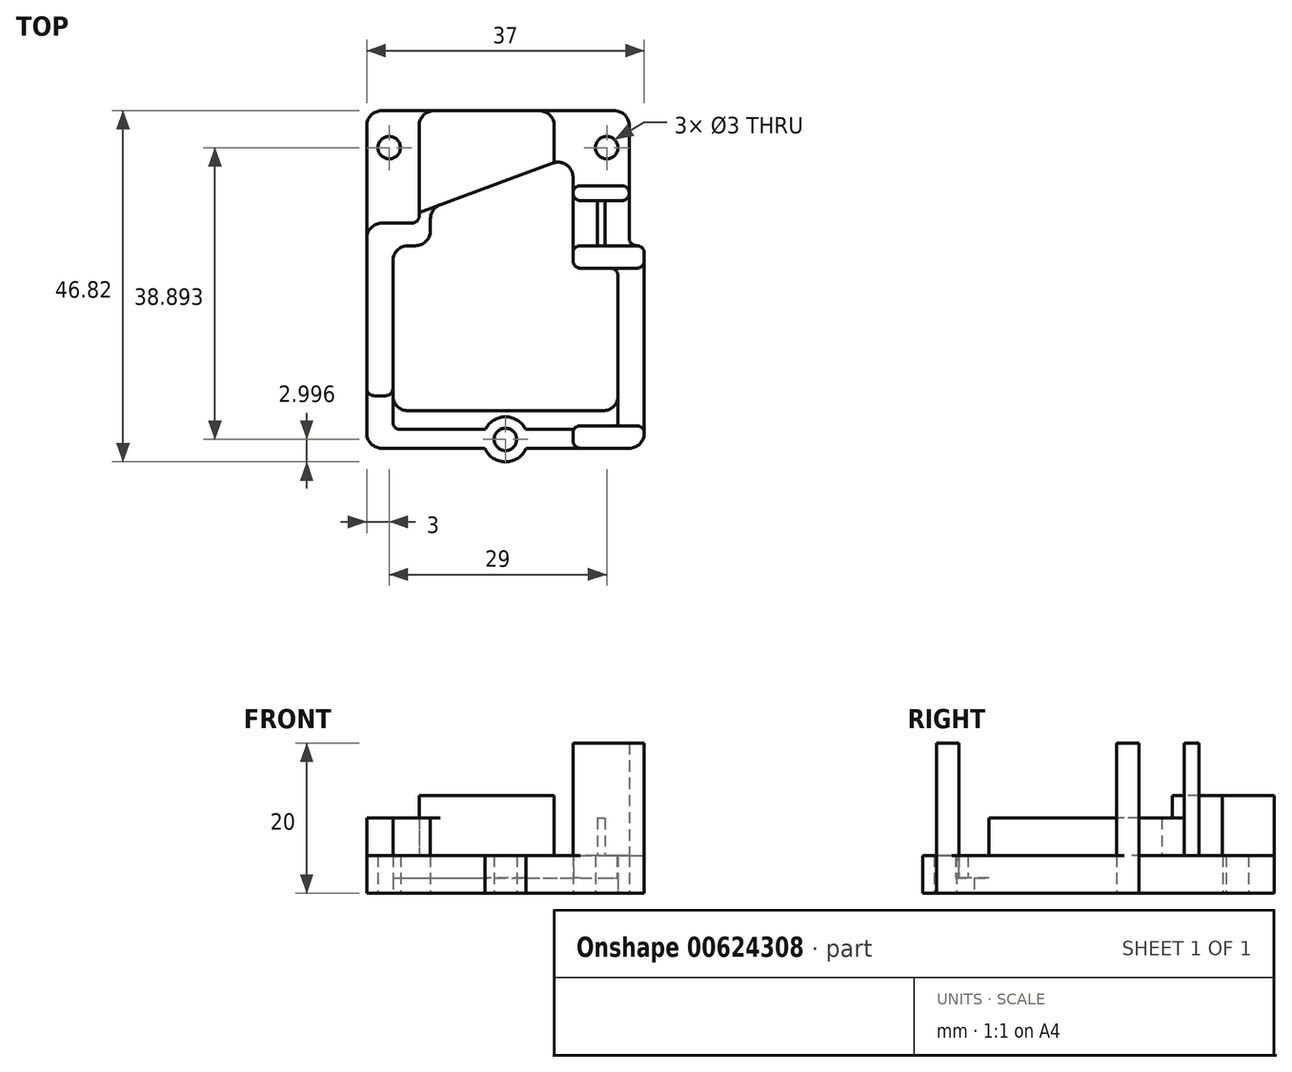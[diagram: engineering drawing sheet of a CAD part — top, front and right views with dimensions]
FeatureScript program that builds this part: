
annotation { "Feature Type Name" : "Feature", "Feature Type Description" : "" }
export const myFeature = defineFeature(function(context is Context, id is Id, definition is map)
    precondition{}
    {
        {
            var Q0;
            Q0=qCreatedBy(makeId("Top.planeOp"),FACE);
            var sketch = newSketch(context, id + "F0", { "sketchPlane" : qUnion([Q0])});
            skLineSegment(sketch, "E0.bottom", {"start": v(16.5, -22.5) * mm, "end": v(-16.5, -22.5) * mm});
            skLineSegment(sketch, "E0.top", {"start": v(14.5, 22.5) * mm, "end": v(-16.5, 22.5) * mm});
            skLineSegment(sketch, "E0.left", {"start": v(18.5, -20.5) * mm, "end": v(18.5, 3.5) * mm});
            skLineSegment(sketch, "E0.right", {"start": v(-18.5, -20.5) * mm, "end": v(-18.5, 20.5) * mm});
            skPoint(sketch, "E0.middle", {"position": v(0, 0) * mm});
            skLineSegment(sketch, "E1", {"start": v(-15, 2.5) * mm, "end": v(-15, -15.5) * mm});
            skLineSegment(sketch, "E2", {"start": v(-13, -17.5) * mm, "end": v(13, -17.5) * mm});
            skLineSegment(sketch, "E3", {"start": v(15, -15.5) * mm, "end": v(15, 0.5) * mm});
            skLineSegment(sketch, "E4", {"start": v(-13, 4.5) * mm, "end": v(-12, 4.5) * mm});
            skLineSegment(sketch, "E5", {"start": v(-10, 6.5) * mm, "end": v(-10, 8.1) * mm});
            skLineSegment(sketch, "E6", {"start": v(-8.7, 9.98) * mm, "end": v(6.3, 15.5) * mm});
            skLineSegment(sketch, "E7", {"start": v(9, 13.63) * mm, "end": v(9, 2.5) * mm});
            skLineSegment(sketch, "E8", {"start": v(10, 1.5) * mm, "end": v(14, 1.5) * mm});
            skLineSegment(sketch, "E9", {"start": v(16.5, 20.5) * mm, "end": v(16.5, 5.5) * mm});
            skLineSegment(sketch, "E10", {"start": v(17.5, 4.5) * mm, "end": v(17.5, 4.5) * mm});
            skPoint(sketch, "E11.visualSharp", {"position": v(-15, -17.5) * mm});
            skArc(sketch, "E11.filletArc", {"start": v(-15, -15.5) * mm, "mid": v(-14.41, -16.91) * mm, "end": v(-13, -17.5) * mm});
            skPoint(sketch, "E12.visualSharp", {"position": v(15, -17.5) * mm});
            skArc(sketch, "E12.filletArc", {"start": v(13, -17.5) * mm, "mid": v(14.41, -16.91) * mm, "end": v(15, -15.5) * mm});
            skPoint(sketch, "E13.visualSharp", {"position": v(-15, 4.5) * mm});
            skArc(sketch, "E13.filletArc", {"start": v(-13, 4.5) * mm, "mid": v(-14.41, 3.91) * mm, "end": v(-15, 2.5) * mm});
            skPoint(sketch, "E14.visualSharp", {"position": v(-10, 4.5) * mm});
            skArc(sketch, "E14.filletArc", {"start": v(-12, 4.5) * mm, "mid": v(-10.59, 5.09) * mm, "end": v(-10, 6.5) * mm});
            skPoint(sketch, "E15.visualSharp", {"position": v(-10, 9.5) * mm});
            skArc(sketch, "E15.filletArc", {"start": v(-8.7, 9.98) * mm, "mid": v(-9.64, 9.25) * mm, "end": v(-10, 8.1) * mm});
            skPoint(sketch, "E16.visualSharp", {"position": v(9, 16.5) * mm});
            skArc(sketch, "E16.filletArc", {"start": v(9, 13.63) * mm, "mid": v(8.14, 15.27) * mm, "end": v(6.3, 15.5) * mm});
            skPoint(sketch, "E17.visualSharp", {"position": v(-18.5, 22.5) * mm});
            skArc(sketch, "E17.filletArc", {"start": v(-16.5, 22.5) * mm, "mid": v(-17.91, 21.91) * mm, "end": v(-18.5, 20.5) * mm});
            skPoint(sketch, "E18.visualSharp", {"position": v(16.5, 22.5) * mm});
            skArc(sketch, "E18.filletArc", {"start": v(16.5, 20.5) * mm, "mid": v(15.91, 21.91) * mm, "end": v(14.5, 22.5) * mm});
            skPoint(sketch, "E19.visualSharp", {"position": v(18.5, -22.5) * mm});
            skArc(sketch, "E19.filletArc", {"start": v(16.5, -22.5) * mm, "mid": v(17.91, -21.91) * mm, "end": v(18.5, -20.5) * mm});
            skPoint(sketch, "E20.visualSharp", {"position": v(-18.5, -22.5) * mm});
            skArc(sketch, "E20.filletArc", {"start": v(-18.5, -20.5) * mm, "mid": v(-17.91, -21.91) * mm, "end": v(-16.5, -22.5) * mm});
            skPoint(sketch, "E21.visualSharp", {"position": v(9, 1.5) * mm});
            skArc(sketch, "E21.filletArc", {"start": v(9, 2.5) * mm, "mid": v(9.3, 1.8) * mm, "end": v(10, 1.5) * mm});
            skPoint(sketch, "E22.visualSharp", {"position": v(15, 1.5) * mm});
            skArc(sketch, "E22.filletArc", {"start": v(15, 0.5) * mm, "mid": v(14.7, 1.2) * mm, "end": v(14, 1.5) * mm});
            skPoint(sketch, "E23.visualSharp", {"position": v(16.5, 4.5) * mm});
            skArc(sketch, "E23.filletArc", {"start": v(16.5, 5.5) * mm, "mid": v(16.8, 4.8) * mm, "end": v(17.5, 4.5) * mm});
            skPoint(sketch, "E24.visualSharp", {"position": v(18.5, 4.5) * mm});
            skArc(sketch, "E24.filletArc", {"start": v(18.5, 3.5) * mm, "mid": v(18.2, 4.2) * mm, "end": v(17.5, 4.5) * mm});
            skLineSegment(sketch, "E25", {"start": v(-14, -20) * mm, "end": v(14, -20) * mm});
            skLineSegment(sketch, "E26", {"start": v(-15, -15.5) * mm, "end": v(-15, -19) * mm});
            skLineSegment(sketch, "E27", {"start": v(15, -15.5) * mm, "end": v(15, -19) * mm});
            skPoint(sketch, "E28.visualSharp", {"position": v(-15, -20) * mm});
            skArc(sketch, "E28.filletArc", {"start": v(-15, -19) * mm, "mid": v(-14.7, -19.7) * mm, "end": v(-14, -20) * mm});
            skPoint(sketch, "E29.visualSharp", {"position": v(15, -20) * mm});
            skArc(sketch, "E29.filletArc", {"start": v(14, -20) * mm, "mid": v(14.7, -19.7) * mm, "end": v(15, -19) * mm});
            skLineSegment(sketch, "E30", {"start": v(0, -17.5) * mm, "end": v(0, -27.49) * mm, "construction": true});
            skPoint(sketch, "E30.endSnap0", {"position": v(0, -22.5) * mm});
            skCircle(sketch, "E31", {"center": v(0, -21.32) * mm, "radius": 3 * mm});
            skCircle(sketch, "E32", {"center": v(0, -21.32) * mm, "radius": 1.5 * mm});
            skCircle(sketch, "E33", {"center": v(-15.5, 17.57) * mm, "radius": 3 * mm});
            skCircle(sketch, "E34", {"center": v(-15.5, 17.57) * mm, "radius": 1.5 * mm});
            skLineSegment(sketch, "E35", {"start": v(-15.5, 17.57) * mm, "end": v(14.82, 17.57) * mm, "construction": true});
            skCircle(sketch, "E36", {"center": v(13.5, 17.57) * mm, "radius": 3 * mm});
            skCircle(sketch, "E37", {"center": v(13.5, 17.57) * mm, "radius": 1.5 * mm});
            skSolve(sketch);
        }
        {
            var Q0;
            Q0=makeQuery(id+"F0.imprint","IMPRINT",FACE,{"disambiguationData":[TD([[makeQuery(id+"F0.imprint","IMPRINT",EDGE,{"derivedFrom":sQuery(id+"F0.wireOp",EDGE,"E2")}),-1.0]])]});
            extrude(context, id + "F1", {"entities" : qUnion([Q0]), "depth" : 2 * mm, "offsetDistance" : 25 * mm});
        }
        {
            var Q0;
            Q0=makeQuery(id+"F0.imprint","IMPRINT",FACE,{"disambiguationData":[TD([[makeQuery(id+"F0.imprint","IMPRINT",EDGE,{"derivedFrom":sQuery(id+"F0.wireOp",EDGE,"E0.top")}),1.0]])]});
            var Q1;
            {var subQ0=sQuery(id+"F0.wireOp",EDGE,"E31");var subQ1=sQuery(id+"F0.wireOp",EDGE,"E25");var subQ2=makeQuery(id+"F0.imprint","INTERSECT",VERTEX,{"disambiguationData":[OD(0.0)],"derivedFrom":[subQ1,subQ0]});Q1=makeQuery(id+"F0.imprint","IMPRINT",FACE,{"disambiguationData":[TD([[makeQuery(id+"F0.imprint","IMPRINT",EDGE,{"disambiguationData":[TD([[subQ2,-1.0]])],"derivedFrom":subQ1}),1.0]])]});}
            var Q2;
            {var subQ0=sQuery(id+"F0.wireOp",EDGE,"E31");var subQ1=sQuery(id+"F0.wireOp",EDGE,"E0.bottom");var subQ2=makeQuery(id+"F0.imprint","INTERSECT",VERTEX,{"disambiguationData":[OD(1.0)],"derivedFrom":[subQ1,subQ0]});Q2=makeQuery(id+"F0.imprint","IMPRINT",FACE,{"disambiguationData":[TD([[makeQuery(id+"F0.imprint","IMPRINT",EDGE,{"disambiguationData":[TD([[subQ2,1.0]])],"derivedFrom":subQ1}),-1.0]])]});}
            var Q3;
            {var subQ0=sQuery(id+"F0.wireOp",EDGE,"E31");var subQ1=sQuery(id+"F0.wireOp",EDGE,"E0.bottom");var subQ2=makeQuery(id+"F0.imprint","INTERSECT",VERTEX,{"disambiguationData":[OD(0.0)],"derivedFrom":[subQ1,subQ0]});Q3=makeQuery(id+"F0.imprint","IMPRINT",FACE,{"disambiguationData":[TD([[makeQuery(id+"F0.imprint","IMPRINT",EDGE,{"disambiguationData":[TD([[subQ2,-1.0]])],"derivedFrom":subQ1}),-1.0]])]});}
            var Q4;
            {var subQ0=sQuery(id+"F0.wireOp",EDGE,"E31");var subQ1=sQuery(id+"F0.wireOp",EDGE,"E0.bottom");var subQ2=makeQuery(id+"F0.imprint","INTERSECT",VERTEX,{"disambiguationData":[OD(0.0)],"derivedFrom":[subQ1,subQ0]});Q4=makeQuery(id+"F0.imprint","IMPRINT",FACE,{"disambiguationData":[TD([[makeQuery(id+"F0.imprint","IMPRINT",EDGE,{"disambiguationData":[TD([[subQ2,-1.0]])],"derivedFrom":subQ1}),1.0]])]});}
            var Q5;
            Q5=makeQuery(id+"F0.imprint","IMPRINT",FACE,{"disambiguationData":[TD([[makeQuery(id+"F0.imprint","IMPRINT",EDGE,{"derivedFrom":sQuery(id+"F0.wireOp",EDGE,"E33")}),1.0]])]});
            var Q6;
            Q6=makeQuery(id+"F0.imprint","IMPRINT",FACE,{"disambiguationData":[TD([[makeQuery(id+"F0.imprint","IMPRINT",EDGE,{"derivedFrom":sQuery(id+"F0.wireOp",EDGE,"E36")}),1.0]])]});
            extrude(context, id + "F2", {"entities" : qUnion([Q0, Q1, Q2, Q3, Q4, Q5, Q6]), "operationType" : NewBodyOperationType.ADD, "depth" : 5 * mm, "offsetDistance" : 25 * mm});
        }
        {
            var Q0;
            Q0=makeQuery(id+"F2.opExtrude","CAP_FACE",FACE,{"disambiguationData":[OSD([sQuery(id+"F0.wireOp",EDGE,"E0.bottom"),sQuery(id+"F0.wireOp",EDGE,"E0.top"),sQuery(id+"F0.wireOp",EDGE,"E0.left"),sQuery(id+"F0.wireOp",EDGE,"E0.right"),sQuery(id+"F0.wireOp",EDGE,"E1"),sQuery(id+"F0.wireOp",EDGE,"E3"),sQuery(id+"F0.wireOp",EDGE,"E4"),sQuery(id+"F0.wireOp",EDGE,"E5"),sQuery(id+"F0.wireOp",EDGE,"E6"),sQuery(id+"F0.wireOp",EDGE,"E7"),sQuery(id+"F0.wireOp",EDGE,"E8"),sQuery(id+"F0.wireOp",EDGE,"E9"),sQuery(id+"F0.wireOp",EDGE,"E13.filletArc"),sQuery(id+"F0.wireOp",EDGE,"E14.filletArc"),sQuery(id+"F0.wireOp",EDGE,"E15.filletArc"),sQuery(id+"F0.wireOp",EDGE,"E16.filletArc"),sQuery(id+"F0.wireOp",EDGE,"E17.filletArc"),sQuery(id+"F0.wireOp",EDGE,"E18.filletArc"),sQuery(id+"F0.wireOp",EDGE,"E19.filletArc"),sQuery(id+"F0.wireOp",EDGE,"E20.filletArc"),sQuery(id+"F0.wireOp",EDGE,"E21.filletArc"),sQuery(id+"F0.wireOp",EDGE,"E22.filletArc"),sQuery(id+"F0.wireOp",EDGE,"E23.filletArc"),sQuery(id+"F0.wireOp",EDGE,"E24.filletArc"),sQuery(id+"F0.wireOp",EDGE,"E25"),sQuery(id+"F0.wireOp",EDGE,"E26"),sQuery(id+"F0.wireOp",EDGE,"E27"),sQuery(id+"F0.wireOp",EDGE,"E28.filletArc"),sQuery(id+"F0.wireOp",EDGE,"E29.filletArc"),sQuery(id+"F0.wireOp",EDGE,"E31"),sQuery(id+"F0.wireOp",EDGE,"E32"),sQuery(id+"F0.wireOp",EDGE,"E34"),sQuery(id+"F0.wireOp",EDGE,"E37")])],"isStart":false});
            var sketch = newSketch(context, id + "F3", { "sketchPlane" : qUnion([Q0])});
            skLineSegment(sketch, "E38", {"start": v(-17.5, -15.5) * mm, "end": v(-16, -15.5) * mm});
            skLineSegment(sketch, "E39", {"start": v(-16.5, 7.5) * mm, "end": v(-12.5, 7.5) * mm});
            skLineSegment(sketch, "E40", {"start": v(-11.5, 8.5) * mm, "end": v(-11.5, 20.5) * mm});
            skLineSegment(sketch, "E41", {"start": v(6.5, 20.5) * mm, "end": v(6.5, 15.58) * mm});
            skLineSegment(sketch, "E42", {"start": v(-9.5, 22.5) * mm, "end": v(4.5, 22.5) * mm});
            skLineSegment(sketch, "E43", {"start": v(6.5, 15.58) * mm, "end": v(-11.5, 8.95) * mm});
            skLineSegment(sketch, "E44", {"start": v(-18.5, 5.5) * mm, "end": v(-18.5, -14.5) * mm});
            skLineSegment(sketch, "E45", {"start": v(-15, -14.5) * mm, "end": v(-15, 2.5) * mm});
            skPoint(sketch, "E46.visualSharp", {"position": v(-11.5, 22.5) * mm});
            skArc(sketch, "E46.filletArc", {"start": v(-9.5, 22.5) * mm, "mid": v(-10.91, 21.91) * mm, "end": v(-11.5, 20.5) * mm});
            skPoint(sketch, "E47.visualSharp", {"position": v(6.5, 22.5) * mm});
            skArc(sketch, "E47.filletArc", {"start": v(6.5, 20.5) * mm, "mid": v(5.91, 21.91) * mm, "end": v(4.5, 22.5) * mm});
            skPoint(sketch, "E48.visualSharp", {"position": v(-18.5, 7.5) * mm});
            skArc(sketch, "E48.filletArc", {"start": v(-16.5, 7.5) * mm, "mid": v(-17.91, 6.91) * mm, "end": v(-18.5, 5.5) * mm});
            skPoint(sketch, "E49.visualSharp", {"position": v(-18.5, -15.5) * mm});
            skArc(sketch, "E49.filletArc", {"start": v(-18.5, -14.5) * mm, "mid": v(-18.2, -15.2) * mm, "end": v(-17.5, -15.5) * mm});
            skPoint(sketch, "E50.visualSharp", {"position": v(-15, -15.5) * mm});
            skArc(sketch, "E50.filletArc", {"start": v(-16, -15.5) * mm, "mid": v(-15.3, -15.2) * mm, "end": v(-15, -14.5) * mm});
            skPoint(sketch, "E51.visualSharp", {"position": v(-11.5, 7.5) * mm});
            skArc(sketch, "E51.filletArc", {"start": v(-12.5, 7.5) * mm, "mid": v(-11.8, 7.8) * mm, "end": v(-11.5, 8.5) * mm});
            skLineSegment(sketch, "E52.bottom", {"start": v(10, 10.5) * mm, "end": v(15.5, 10.5) * mm});
            skLineSegment(sketch, "E52.top", {"start": v(10, 12.5) * mm, "end": v(15.5, 12.5) * mm});
            skLineSegment(sketch, "E52.left", {"start": v(9, 11.5) * mm, "end": v(9, 11.5) * mm});
            skLineSegment(sketch, "E52.right", {"start": v(16.5, 11.5) * mm, "end": v(16.5, 11.5) * mm});
            skLineSegment(sketch, "E53.bottom", {"start": v(10, 1.5) * mm, "end": v(17.5, 1.5) * mm});
            skLineSegment(sketch, "E53.top", {"start": v(10, 4.5) * mm, "end": v(17.5, 4.5) * mm});
            skLineSegment(sketch, "E53.left", {"start": v(9, 2.5) * mm, "end": v(9, 3.5) * mm});
            skLineSegment(sketch, "E53.right", {"start": v(18.5, 2.5) * mm, "end": v(18.5, 3.5) * mm});
            skLineSegment(sketch, "E54.bottom", {"start": v(10, -22.5) * mm, "end": v(16.5, -22.5) * mm});
            skLineSegment(sketch, "E54.top", {"start": v(10, -19.5) * mm, "end": v(17.5, -19.5) * mm});
            skLineSegment(sketch, "E54.left", {"start": v(9, -21.5) * mm, "end": v(9, -20.5) * mm});
            skLineSegment(sketch, "E54.right", {"start": v(18.5, -20.5) * mm, "end": v(18.5, -20.5) * mm});
            skLineSegment(sketch, "E55.bottom", {"start": v(13.25, 1.5) * mm, "end": v(12.25, 1.5) * mm});
            skLineSegment(sketch, "E55.left", {"start": v(13.25, 4.5) * mm, "end": v(13.25, 10.5) * mm});
            skLineSegment(sketch, "E55.right", {"start": v(12.25, 4.5) * mm, "end": v(12.25, 10.5) * mm});
            skPoint(sketch, "E55.middle", {"position": v(12.75, 10.5) * mm});
            skPoint(sketch, "E56.visualSharp", {"position": v(9, 12.5) * mm});
            skArc(sketch, "E56.filletArc", {"start": v(10, 12.5) * mm, "mid": v(9.3, 12.2) * mm, "end": v(9, 11.5) * mm});
            skPoint(sketch, "E57.visualSharp", {"position": v(9, 10.5) * mm});
            skArc(sketch, "E57.filletArc", {"start": v(9, 11.5) * mm, "mid": v(9.3, 10.8) * mm, "end": v(10, 10.5) * mm});
            skPoint(sketch, "E58.visualSharp", {"position": v(16.5, 10.5) * mm});
            skArc(sketch, "E58.filletArc", {"start": v(15.5, 10.5) * mm, "mid": v(16.2, 10.8) * mm, "end": v(16.5, 11.5) * mm});
            skPoint(sketch, "E59.visualSharp", {"position": v(16.5, 12.5) * mm});
            skArc(sketch, "E59.filletArc", {"start": v(16.5, 11.5) * mm, "mid": v(16.2, 12.2) * mm, "end": v(15.5, 12.5) * mm});
            skPoint(sketch, "E60.visualSharp", {"position": v(9, 4.5) * mm});
            skArc(sketch, "E60.filletArc", {"start": v(10, 4.5) * mm, "mid": v(9.3, 4.2) * mm, "end": v(9, 3.5) * mm});
            skPoint(sketch, "E61.visualSharp", {"position": v(18.5, 1.5) * mm});
            skArc(sketch, "E61.filletArc", {"start": v(17.5, 1.5) * mm, "mid": v(18.2, 1.8) * mm, "end": v(18.5, 2.5) * mm});
            skPoint(sketch, "E62.visualSharp", {"position": v(9, 1.5) * mm});
            skArc(sketch, "E62.filletArc", {"start": v(9, 2.5) * mm, "mid": v(9.3, 1.8) * mm, "end": v(10, 1.5) * mm});
            skPoint(sketch, "E63.visualSharp", {"position": v(18.5, 4.5) * mm});
            skArc(sketch, "E63.filletArc", {"start": v(18.5, 3.5) * mm, "mid": v(18.2, 4.2) * mm, "end": v(17.5, 4.5) * mm});
            skPoint(sketch, "E64.visualSharp", {"position": v(18.5, -19.5) * mm});
            skArc(sketch, "E64.filletArc", {"start": v(18.5, -20.5) * mm, "mid": v(18.2, -19.8) * mm, "end": v(17.5, -19.5) * mm});
            skPoint(sketch, "E65.visualSharp", {"position": v(9, -19.5) * mm});
            skArc(sketch, "E65.filletArc", {"start": v(10, -19.5) * mm, "mid": v(9.3, -19.8) * mm, "end": v(9, -20.5) * mm});
            skPoint(sketch, "E66.visualSharp", {"position": v(9, -22.5) * mm});
            skArc(sketch, "E66.filletArc", {"start": v(9, -21.5) * mm, "mid": v(9.3, -22.2) * mm, "end": v(10, -22.5) * mm});
            skPoint(sketch, "E67.visualSharp", {"position": v(18.5, -22.5) * mm});
            skArc(sketch, "E67.filletArc", {"start": v(16.5, -22.5) * mm, "mid": v(17.91, -21.91) * mm, "end": v(18.5, -20.5) * mm});
            skSolve(sketch);
        }
        {
            var Q0;
            Q0=makeQuery(id+"F3.imprint","IMPRINT",FACE,{"disambiguationData":[TD([[makeQuery(id+"F3.imprint","IMPRINT",EDGE,{"derivedFrom":sQuery(id+"F3.wireOp",EDGE,"E38")}),1.0]])]});
            extrude(context, id + "F4", {"entities" : qUnion([Q0]), "operationType" : NewBodyOperationType.ADD, "depth" : 5 * mm, "offsetDistance" : 25 * mm});
        }
        {
            var Q0;
            {var subQ2=sQuery(id+"F3.wireOp",EDGE,"E41");Q0=makeQuery(id+"F3.imprint","IMPRINT",FACE,{"disambiguationData":[TD([[makeQuery(id+"F3.imprint","IMPRINT",EDGE,{"derivedFrom":subQ2}),-1.0]])]});}
            extrude(context, id + "F5", {"entities" : qUnion([Q0]), "operationType" : NewBodyOperationType.ADD, "depth" : 8 * mm, "offsetDistance" : 25 * mm});
        }
        {
            var Q0;
            {var subQ0=sQuery(id+"F3.wireOp",EDGE,"E65.filletArc");var subQ1=sQuery(id+"F3.wireOp",EDGE,"E54.top");var subQ2=makeQuery(id+"F3.imprint","INTERSECT",VERTEX,{"derivedFrom":[subQ1,subQ0]});Q0=makeQuery(id+"F3.imprint","IMPRINT",FACE,{"disambiguationData":[TD([[makeQuery(id+"F3.imprint","IMPRINT",EDGE,{"disambiguationData":[TD([[subQ2,-1.0]])],"derivedFrom":subQ1}),-1.0]])]});}
            var Q1;
            Q1=makeQuery(id+"F3.imprint","IMPRINT",FACE,{"disambiguationData":[TD([[makeQuery(id+"F3.imprint","IMPRINT",EDGE,{"derivedFrom":sQuery(id+"F3.wireOp",EDGE,"E54.bottom")}),-1.0]])]});
            extrude(context, id + "F6", {"entities" : qUnion([Q0, Q1]), "operationType" : NewBodyOperationType.ADD, "oppositeDirection" : true, "depth" : 4 * mm, "offsetDistance" : 25 * mm});
        }
        {
            var Q0;
            {var subQ0=sQuery(id+"F3.wireOp",EDGE,"E65.filletArc");var subQ1=sQuery(id+"F3.wireOp",EDGE,"E54.top");var subQ2=makeQuery(id+"F3.imprint","INTERSECT",VERTEX,{"derivedFrom":[subQ1,subQ0]});Q0=makeQuery(id+"F3.imprint","IMPRINT",FACE,{"disambiguationData":[TD([[makeQuery(id+"F3.imprint","IMPRINT",EDGE,{"disambiguationData":[TD([[subQ2,-1.0]])],"derivedFrom":subQ1}),-1.0]])]});}
            var Q1;
            Q1=makeQuery(id+"F3.imprint","IMPRINT",FACE,{"disambiguationData":[TD([[makeQuery(id+"F3.imprint","IMPRINT",EDGE,{"derivedFrom":sQuery(id+"F3.wireOp",EDGE,"E54.bottom")}),-1.0]])]});
            extrude(context, id + "F7", {"entities" : qUnion([Q0, Q1]), "operationType" : NewBodyOperationType.ADD, "depth" : 15 * mm, "offsetDistance" : 25 * mm});
        }
        {
            var Q0;
            Q0=makeQuery(id+"F3.imprint","IMPRINT",FACE,{"disambiguationData":[TD([[makeQuery(id+"F3.imprint","IMPRINT",EDGE,{"derivedFrom":sQuery(id+"F3.wireOp",EDGE,"E53.left")}),1.0]])]});
            var Q1;
            Q1=makeQuery(id+"F3.imprint","IMPRINT",FACE,{"disambiguationData":[TD([[makeQuery(id+"F3.imprint","IMPRINT",EDGE,{"derivedFrom":sQuery(id+"F3.wireOp",EDGE,"E52.top")}),-1.0]])]});
            extrude(context, id + "F8", {"entities" : qUnion([Q0, Q1]), "operationType" : NewBodyOperationType.ADD, "depth" : 15 * mm, "offsetDistance" : 25 * mm});
        }
        {
            var Q0;
            {var subQ0=sQuery(id+"F3.wireOp",EDGE,"E55.left");Q0=makeQuery(id+"F3.imprint","IMPRINT",FACE,{"disambiguationData":[TD([[makeQuery(id+"F3.imprint","IMPRINT",EDGE,{"derivedFrom":subQ0}),1.0]])]});}
            extrude(context, id + "F9", {"entities" : qUnion([Q0]), "operationType" : NewBodyOperationType.ADD, "depth" : 5 * mm, "offsetDistance" : 25 * mm});
        }
    });
